# Revit family: Kugelhahn mit Verlängerung und Hebelgriff 2190
name_source: partatom
category: Rohrzubehör
revit_build: Autodesk Revit 2018 (Build: 20190510_1515(x64)
units: mm (PartAtom-declared; Revit-internal decimal feet)

## family parameters
Arbeitsebenenbasiert = Nein
Beim Laden mit Abzugskörper schneiden = Nein
Bemaßung runder Anschluss = Durchmesser verwenden
Gemeinsam genutzt = Nein
Immer vertikal = Ja
OmniClass-Nummer = 23.65.55.14
OmniClass-Titel = Valves for Liquid Services
Teiletyp = Unterbricht

## types (1)
- Kugelhahn mit Verlängerung und Hebelgriff 2190
    Anwendungen = Der Kugelhahn mit verlängerten Spindel DRZ wird in der Installationen als Absperreinrichtung verwendet.
Anwendungsgebiete sind Zentralheizungs- und Kälteanlagenlagen.
Die verlängerte Spindel erleichtert das Anbringen der Isolierung.
Der Griff ist separat zu isolieren sodass es beim Öffnen und Schließen zu keinen Beschädigung der Isolierung kommt.
Der HERZ-Kugelhahn mit verlängerten Spindel DZR ist aus dem Werkstoff CW602N.
Der Kugelhahn ist bidirektional, das heißt, beide Fließrichtungen sind möglich.
    Einsatzbereich = Kugelhähne werden zum Absperren von Leitungen und Anlagen verwendet.
Einsatzbereiche sind Heizungs- und Kälteanlagen.
Der Kugelhahn ist nicht geeignet für die Durchflussregelung und muss immer in voll geöffneter oder geschlossener Position verwendet werden.
    Gehäuse = geschmiedetes Messing EN 12165, CW602N DZR
    Griff = Hebelgriff rot, Stahlblech beschichtet
    Hersteller = HERZ Armaturen Ges.m.b.H
    Innengewinde = nach ISO 228
    Konstruktion und Prüfungen = WRAS geprüft
    Kugel = geschmiedetes Messing EN 12165, voller Durchgang verchromt, CW617N
    Kugeldichtung = PTFE
    Max.Betriebsdruck (DN15-DN25) = 2500000.0 Pa
    Max.Betriebstemperatur = 130 °C
    Max.Betriebstemperatur (Wasser - kein Dampf) = 110 °C
    Max.Betriebstemperatur Kurzzeitbelastung = 150 °C
    Medium = Heizungswasserqualität nach ÖNORM H 5195 oder VDI-Richtline 2035.
Die Verwendung von Ethylen- oder Propylenglykol in einem Mischungsverhältnis 25 - 50% ist zulässig.
    Min.Betriebstemperatur = -10 °C
    Min.Betriebstemperatur (Wasser) = 1 °C
    Min.Betriebstemperatur Kurzzeitbelastung = -50 °C
    SCRNCODE = 05;10;02
    SCRNSEQ = ARM;ARM_TYP="ABVS";2
    Spindel = Messing nach EN 12164, CW614N
    Spindeldichtung = EPDM
    URL = www.herz-armaturen.at
    W01 = 135.00°
